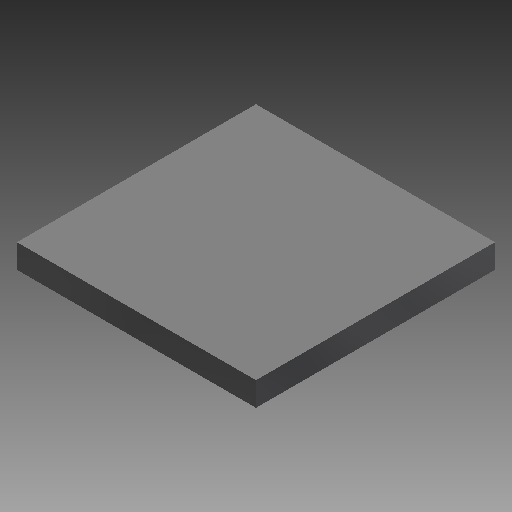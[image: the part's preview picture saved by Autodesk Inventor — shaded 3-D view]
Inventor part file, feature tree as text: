
AUTODESK INVENTOR PART (.ipt)
format: ipt  version: 2017 (Build 210142000, 142)  size: 93,184 bytes
history: native  units: in
note: dims shown in document units (in); Inventor stores cm internally (conversion verified against a paired STEP export)
features: extrude x1, sketch x1
ambient origin geometry x8: Origin, YZ Plane, XZ Plane, XY Plane, X Axis, Y Axis, Z Axis, Center Point
bodies: Solid1 (feature_tree)
feature tree (2):
  extrude  "Extrusion1"  Depth=1.0in
  sketch  "Sketch1"  dims[d0=1.0in d2=1.0in d3=0.1in d4=0.0in]
